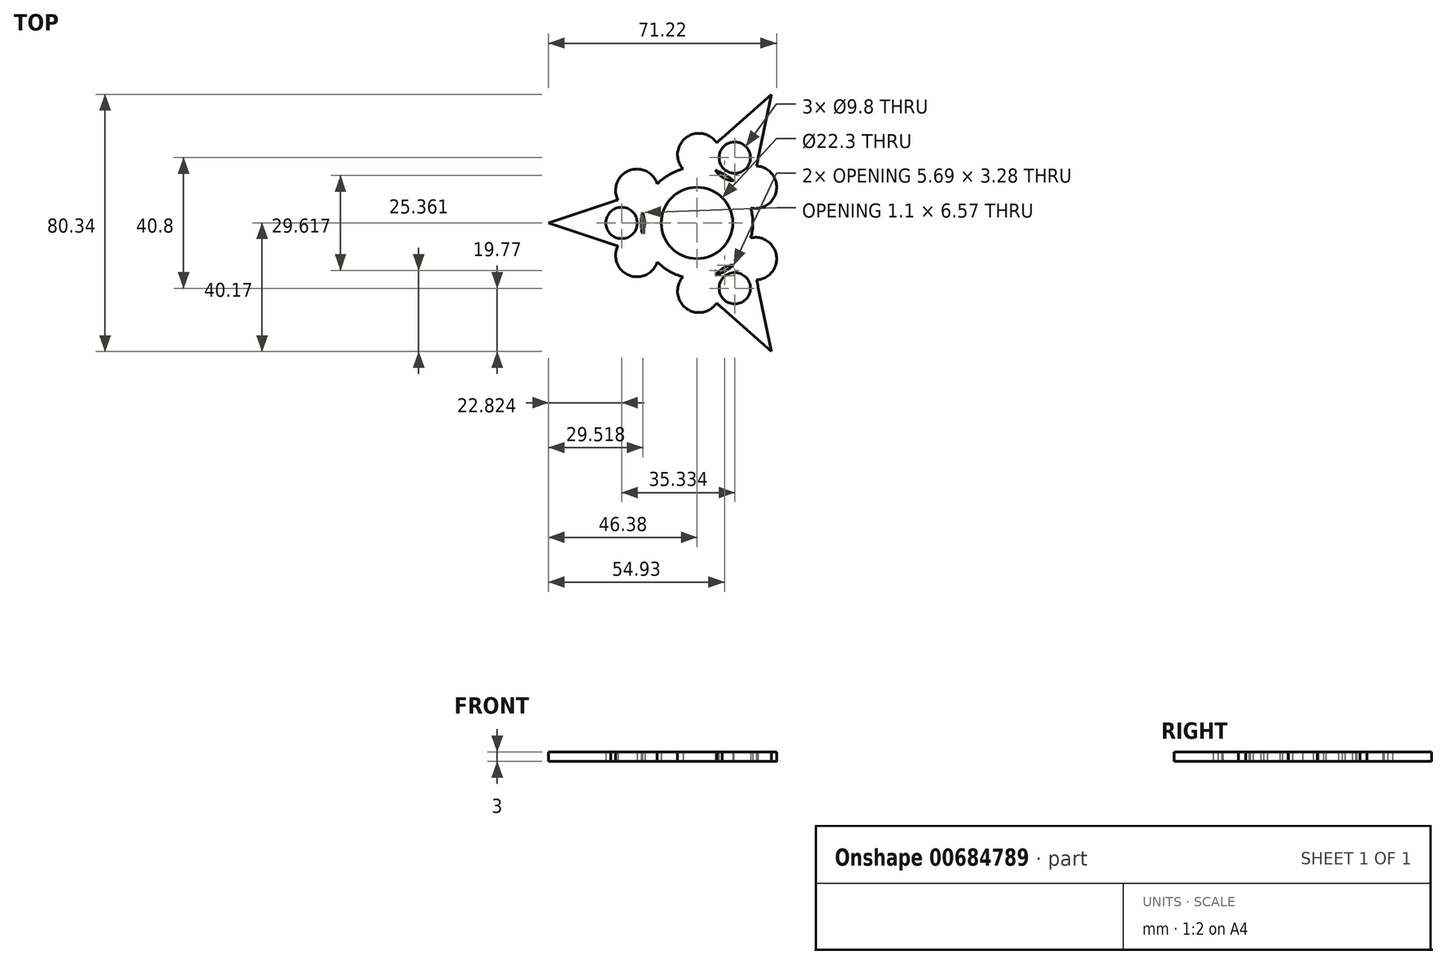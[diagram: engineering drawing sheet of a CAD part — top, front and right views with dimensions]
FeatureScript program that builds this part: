
annotation { "Feature Type Name" : "Feature", "Feature Type Description" : "" }
export const myFeature = defineFeature(function(context is Context, id is Id, definition is map)
    precondition{}
    {
        {
            var Q0;
            Q0=qCreatedBy(makeId("Top.planeOp"),FACE);
            var sketch = newSketch(context, id + "F0", { "sketchPlane" : qUnion([Q0])});
            skCircle(sketch, "E0", {"center": v(0, 0) * mm, "radius": 11.15 * mm});
            skCircle(sketch, "E1", {"center": v(0, 0) * mm, "radius": 17.41 * mm});
            skCircle(sketch, "E2", {"center": v(-23.56, 0) * mm, "radius": 4.9 * mm});
            skCircle(sketch, "E3", {"center": v(-23.56, 0) * mm, "radius": 7.24 * mm});
            skArc(sketch, "E4", {"start": v(-24.7, -7.15) * mm, "mid": v(-21.3, -16.32) * mm, "end": v(-12.42, -12.2) * mm});
            skArc(sketch, "E5.MirrorCS", {"start": v(-24.7, 7.15) * mm, "mid": v(-21.3, 16.32) * mm, "end": v(-12.42, 12.2) * mm});
            skLineSegment(sketch, "E6", {"start": v(-24.7, 7.15) * mm, "end": v(-46.38, 0) * mm});
            skLineSegment(sketch, "E7", {"start": v(-46.38, 0) * mm, "end": v(-24.7, -7.15) * mm});
            skCircle(sketch, "E8.1.0", {"center": v(11.78, -20.4) * mm, "radius": 4.9 * mm});
            skCircle(sketch, "E8.1.1", {"center": v(11.78, -20.4) * mm, "radius": 7.24 * mm});
            skLineSegment(sketch, "E8.1.2", {"start": v(6.16, -24.97) * mm, "end": v(23.2, -40.17) * mm});
            skArc(sketch, "E8.1.3", {"start": v(18.54, -17.81) * mm, "mid": v(24.78, -10.28) * mm, "end": v(16.78, -4.65) * mm});
            skLineSegment(sketch, "E8.1.4", {"start": v(23.2, -40.17) * mm, "end": v(18.54, -17.81) * mm});
            skArc(sketch, "E8.1.5", {"start": v(6.16, -24.97) * mm, "mid": v(-3.5, -26.6) * mm, "end": v(-4.36, -16.86) * mm});
            skCircle(sketch, "E8.2.0", {"center": v(11.78, 20.4) * mm, "radius": 4.9 * mm});
            skCircle(sketch, "E8.2.1", {"center": v(11.78, 20.4) * mm, "radius": 7.24 * mm});
            skLineSegment(sketch, "E8.2.2", {"start": v(18.54, 17.81) * mm, "end": v(23.2, 40.17) * mm});
            skArc(sketch, "E8.2.3", {"start": v(6.16, 24.97) * mm, "mid": v(-3.5, 26.6) * mm, "end": v(-4.36, 16.86) * mm});
            skLineSegment(sketch, "E8.2.4", {"start": v(23.2, 40.17) * mm, "end": v(6.16, 24.97) * mm});
            skArc(sketch, "E8.2.5", {"start": v(18.54, 17.81) * mm, "mid": v(24.78, 10.28) * mm, "end": v(16.78, 4.65) * mm});
            skSolve(sketch);
        }
        {
            var Q0;
            Q0 = qSketchRegion(id + "F0", true);
            extrude(context, id + "F1", {"entities" : qUnion([Q0]), "depth" : 3 * mm, "offsetDistance" : 25 * mm});
        }
    });
